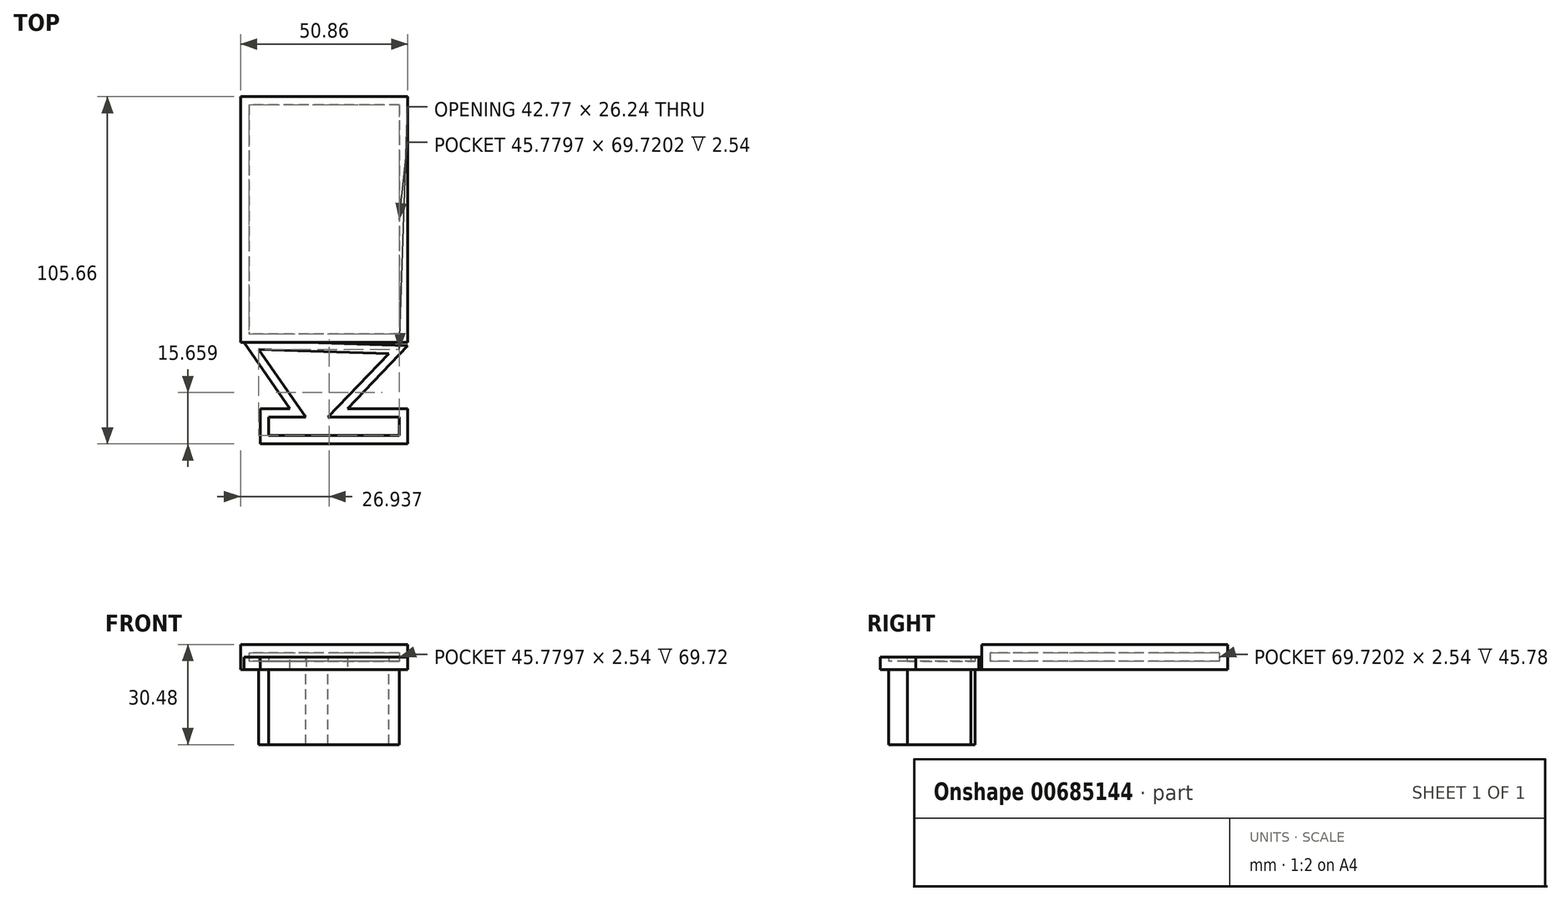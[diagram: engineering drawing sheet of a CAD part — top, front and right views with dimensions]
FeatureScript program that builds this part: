
annotation { "Feature Type Name" : "Feature", "Feature Type Description" : "" }
export const myFeature = defineFeature(function(context is Context, id is Id, definition is map)
    precondition{}
    {
        {
            var Q0;
            Q0=qCreatedBy(makeId("Top.planeOp"),FACE);
            var sketch = newSketch(context, id + "F0", { "sketchPlane" : qUnion([Q0])});
            skLineSegment(sketch, "E0.bottom", {"start": v(0, 0) * mm, "end": v(-50.86, 0) * mm});
            skLineSegment(sketch, "E0.top", {"start": v(0, -74.8) * mm, "end": v(-50.86, -74.8) * mm});
            skLineSegment(sketch, "E0.left", {"start": v(0, 0) * mm, "end": v(0, -74.8) * mm});
            skLineSegment(sketch, "E0.right", {"start": v(-50.86, 0) * mm, "end": v(-50.86, -74.8) * mm});
            skSolve(sketch);
        }
        {
            var Q0;
            Q0=makeQuery(id+"F0.imprint","IMPRINT",FACE,{"disambiguationData":[TD([[makeQuery(id+"F0.imprint","IMPRINT",EDGE,{"derivedFrom":sQuery(id+"F0.wireOp",EDGE,"E0.bottom")}),1.0]])]});
            extrude(context, id + "F1", {"entities" : qUnion([Q0]), "depth" : 7.62 * mm, "offsetDistance" : 25.4 * mm});
        }
        {
            var Q0;
            Q0=qCreatedBy(makeId("Top.planeOp"),FACE);
            var sketch = newSketch(context, id + "F2", { "sketchPlane" : qUnion([Q0])});
            skLineSegment(sketch, "E1", {"start": v(-50.27, -74.18) * mm, "end": v(-28.5, -105.58) * mm});
            skLineSegment(sketch, "E2", {"start": v(-28.5, -105.58) * mm, "end": v(0, -75.78) * mm});
            skLineSegment(sketch, "E3", {"start": v(0, -75.78) * mm, "end": v(-50.27, -74.18) * mm});
            skSolve(sketch);
        }
        {
            var Q0;
            Q0=qCreatedBy(makeId("Top.planeOp"),FACE);
            var sketch = newSketch(context, id + "F3", { "sketchPlane" : qUnion([Q0])});
            skLineSegment(sketch, "E4.bottom", {"start": v(-28.47, -105.66) * mm, "end": v(0, -105.66) * mm});
            skLineSegment(sketch, "E4.top", {"start": v(-28.47, -94.96) * mm, "end": v(0, -94.96) * mm});
            skLineSegment(sketch, "E4.left", {"start": v(-28.47, -105.66) * mm, "end": v(-28.47, -94.96) * mm});
            skLineSegment(sketch, "E4.right", {"start": v(0, -105.66) * mm, "end": v(0, -94.96) * mm});
            skLineSegment(sketch, "E5.bottom", {"start": v(-44.84, -94.96) * mm, "end": v(-28.47, -94.96) * mm});
            skLineSegment(sketch, "E5.top", {"start": v(-44.84, -105.66) * mm, "end": v(-28.47, -105.66) * mm});
            skLineSegment(sketch, "E5.left", {"start": v(-44.84, -94.96) * mm, "end": v(-44.84, -105.66) * mm});
            skLineSegment(sketch, "E5.right", {"start": v(-28.47, -94.96) * mm, "end": v(-28.47, -105.66) * mm});
            skLineSegment(sketch, "E6.bottom", {"start": v(-44.84, -94.96) * mm, "end": v(-54.49, -94.96) * mm});
            skLineSegment(sketch, "E6.top", {"start": v(-44.84, -105.66) * mm, "end": v(-54.49, -105.66) * mm});
            skLineSegment(sketch, "E6.right", {"start": v(-54.49, -94.96) * mm, "end": v(-54.49, -105.66) * mm});
            skSolve(sketch);
        }
        {
            var Q0;
            Q0=makeQuery(id+"F2.imprint","IMPRINT",FACE,{"disambiguationData":[TD([[makeQuery(id+"F2.imprint","IMPRINT",EDGE,{"derivedFrom":sQuery(id+"F2.wireOp",EDGE,"E1")}),1.0]])]});
            extrude(context, id + "F4", {"entities" : qUnion([Q0]), "operationType" : NewBodyOperationType.ADD, "depth" : 3.8 * mm, "offsetDistance" : 25.4 * mm});
        }
        {
            var Q0;
            Q0=makeQuery(id+"F3.imprint","IMPRINT",FACE,{"disambiguationData":[TD([[makeQuery(id+"F3.imprint","IMPRINT",EDGE,{"derivedFrom":sQuery(id+"F3.wireOp",EDGE,"E4.bottom")}),1.0]])]});
            var Q1;
            Q1=makeQuery(id+"F3.imprint","IMPRINT",FACE,{"disambiguationData":[TD([[makeQuery(id+"F3.imprint","IMPRINT",EDGE,{"derivedFrom":sQuery(id+"F3.wireOp",EDGE,"E5.bottom")}),-1.0]])]});
            extrude(context, id + "F5", {"entities" : qUnion([Q0, Q1]), "operationType" : NewBodyOperationType.ADD, "depth" : 3.8 * mm, "offsetDistance" : 25.4 * mm});
        }
        {
            var Q0;
            Q0=makeQuery(id+"F5.boolean.opBoolean","MERGE",FACE,{"derivedFrom":[makeQuery(id+"F4.opExtrude","CAP_FACE",FACE,{"disambiguationData":[OSD([sQuery(id+"F2.wireOp",EDGE,"E1"),sQuery(id+"F2.wireOp",EDGE,"E2"),sQuery(id+"F2.wireOp",EDGE,"E3")])],"isStart":false}),makeQuery(id+"F5.opExtrude","CAP_FACE",FACE,{"disambiguationData":[OSD([sQuery(id+"F3.wireOp",EDGE,"E4.bottom"),sQuery(id+"F3.wireOp",EDGE,"E4.top"),sQuery(id+"F3.wireOp",EDGE,"E4.right"),sQuery(id+"F3.wireOp",EDGE,"E5.bottom"),sQuery(id+"F3.wireOp",EDGE,"E5.top"),sQuery(id+"F3.wireOp",EDGE,"E5.left")])],"isStart":false})]});
            shell(context, id + "F6", {"entities" : qUnion([Q0]), "thickness" : 2.54 * mm});
        }
        {
            var Q0;
            Q0=makeQuery(id+"F6.opShell","OFFSET_FACE",FACE,{"disambiguationData":[OSD([sQuery(id+"F0.wireOp",EDGE,"E0.bottom"),sQuery(id+"F0.wireOp",EDGE,"E0.top"),sQuery(id+"F0.wireOp",EDGE,"E0.left"),sQuery(id+"F0.wireOp",EDGE,"E0.right"),sQuery(id+"F2.wireOp",EDGE,"E1"),sQuery(id+"F2.wireOp",EDGE,"E2"),sQuery(id+"F2.wireOp",EDGE,"E3"),sQuery(id+"F3.wireOp",EDGE,"E4.bottom"),sQuery(id+"F3.wireOp",EDGE,"E4.top"),sQuery(id+"F3.wireOp",EDGE,"E4.right"),sQuery(id+"F3.wireOp",EDGE,"E5.bottom"),sQuery(id+"F3.wireOp",EDGE,"E5.top"),sQuery(id+"F3.wireOp",EDGE,"E5.left")]),OD(1.0)]});
            extrude(context, id + "F7", {"entities" : qUnion([Q0]), "operationType" : NewBodyOperationType.ADD, "oppositeDirection" : true, "depth" : 25.4 * mm, "offsetDistance" : 25.4 * mm});
        }
    });
